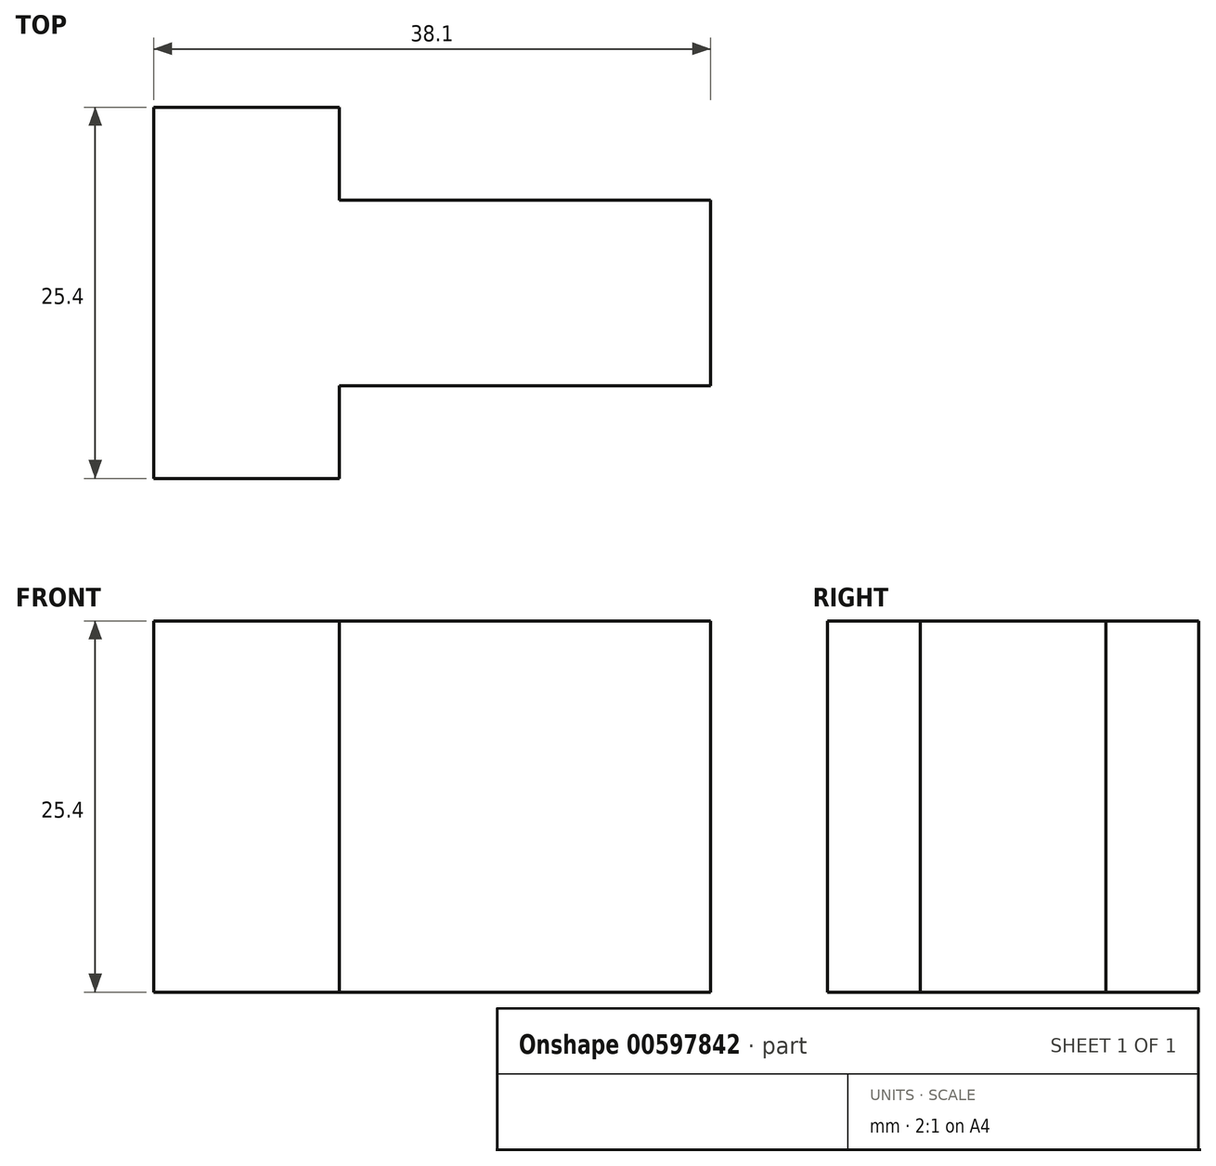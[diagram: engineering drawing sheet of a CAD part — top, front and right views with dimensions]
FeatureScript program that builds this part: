
annotation { "Feature Type Name" : "Feature", "Feature Type Description" : "" }
export const myFeature = defineFeature(function(context is Context, id is Id, definition is map)
    precondition{}
    {
        {
            var Q0;
            Q0=qCreatedBy(makeId("Top.planeOp"),FACE);
            var sketch = newSketch(context, id + "F0", { "sketchPlane" : qUnion([Q0])});
            skLineSegment(sketch, "E0", {"start": v(0, 0) * mm, "end": v(0, 25.4) * mm});
            skLineSegment(sketch, "E1", {"start": v(0, 0) * mm, "end": v(12.7, 0) * mm});
            skLineSegment(sketch, "E2", {"start": v(0, 25.4) * mm, "end": v(12.7, 25.4) * mm});
            skLineSegment(sketch, "E3", {"start": v(12.7, 25.4) * mm, "end": v(12.7, 19.05) * mm});
            skLineSegment(sketch, "E4", {"start": v(12.7, 0) * mm, "end": v(12.7, 6.35) * mm});
            skLineSegment(sketch, "E5", {"start": v(12.7, 6.35) * mm, "end": v(38.1, 6.35) * mm});
            skLineSegment(sketch, "E6", {"start": v(12.7, 19.05) * mm, "end": v(38.1, 19.05) * mm});
            skLineSegment(sketch, "E7", {"start": v(38.1, 19.05) * mm, "end": v(38.1, 6.35) * mm});
            skSolve(sketch);
        }
        {
            var Q0;
            Q0=makeQuery(id+"F0.imprint","IMPRINT",FACE,{"disambiguationData":[TD([[makeQuery(id+"F0.imprint","IMPRINT",EDGE,{"derivedFrom":sQuery(id+"F0.wireOp",EDGE,"E0")}),-1.0]])]});
            extrude(context, id + "F1", {"entities" : qUnion([Q0]), "depth" : 25.4 * mm, "offsetDistance" : 25.4 * mm});
        }
    });
